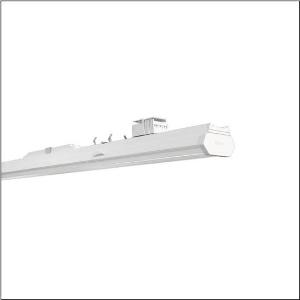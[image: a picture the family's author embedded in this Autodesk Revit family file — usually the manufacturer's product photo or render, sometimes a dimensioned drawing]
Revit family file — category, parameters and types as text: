
# Revit family: licross_21_protected_ho_52td11dn4axs
name_source: partatom
category: Lighting Fixtures
units: mm (PartAtom-declared; Revit-internal decimal feet)

## family parameters
Cut with Voids When Loaded = No
Host = Face
Light Source = No
Part Type = Normal
Room Calculation Point = No
Round Connector Dimension = Use Diameter
Shared = No

## types (1)
- --- (1 x LED, 10000 lm, 55.1 W, 4000K)
    Apparent Load = 55 VA
    CIE Flux Codes = 84 94 98 99 100
    Color Rendering = 80
    Color Temperature = 4000K
    Default Elevation = 1800 mm
    Description = Licross 21 Protected HO, luminaire insert, of sheet steel, galvanised, coil coated, white, length: 1.500mm, width: 90mm, height: 103mm, LED rated luminous flux: 10.000lm, light colour: 840, SDCM (Standard Deviation of Colour Matching)MacAdam ≤ 3 SDCM (initial), control gear: DALI 2, with plug, 5-pole, with phase selection, mains connection: 220..240V, AC, 50/60Hz, rated input power: 55W, internal wiring halogen-free, primary light control with lens, of plastic, primary optical cover: cover, of PMMA, light emission: direct distribution, primary light characteristic: symmetric, protection rating (complete): IP54, insulation class (complete): insulation class I (protective earthing), certification: CE, ENEC, VDE, UKCA, protection symbol: D if used in an environment with non-conductive dust loads with corresponding accessories, impact resistance: IK06, permissible ambient temperature for indoor applications: -25..+45°C, corresponds to IFS (International Featured Standards) requirements for safety and quality in the food industry, reducing of maximum allowable ambient temperature of 5°C with ceiling mounting, LABS conformity tested according to VDMA 24364:2018-05, The light source and the operating device comply with the requirements of the Ecodesign Regulation (EU) 2019/2020 and are replaceable in accordance with this regulation, packaging unit: 1 piece
    Height = 92 mm
    Lamp = 1 x LED
    Lamp Light Flux = 10000 lm
    Lamp Power = 55.1 W
    Lamp count = 1
    Length = 1500 mm
    Luminous efficacy = 181 lm/W
    Manufacturer = Siteco
    ModVariant = No
    Model = 52TD11DN4AXS
    Mounting Place = Ceiling
    Mounting Type = Pendant
    Number of Poles = 1
    OnlyDefault = Yes
    Power Factor = 1
    Product Name = Licross 21 Protected HO
    Product group = luminaire insert | ceiling pendant
    ProductGroupID = 901
    Protection Class = Protection class I
    Protection Degree = IP 54
    RLX_Detail_Level = 1
    RLX_Emergency_Light_Flux = 0 lm
    RLX_Emergency_Type = 0
    RLX_Emergency_Type_DB = No
    RlxData = <blob elided: 24441 chars, md5=7d5eab98>
    Socket = socket
    Standby Power = 0 W
    System Light Flux = 10000 lm
    System Power = 55 W
    Type Comments = factory setting: luminous flux: 100 % | dim-lin: 254 | 316 mA
    Type Image = l_1256148.jpg
    URL = http://relux.com
    VarID = @adj_130231
    Voltage = 0 V
    Weight = 0.00 kg
    Width = 88 mm

## geometry (parser evidence)
native form markers: Blend x4, Sweep x10
no freeform markers — native parametric forms only
